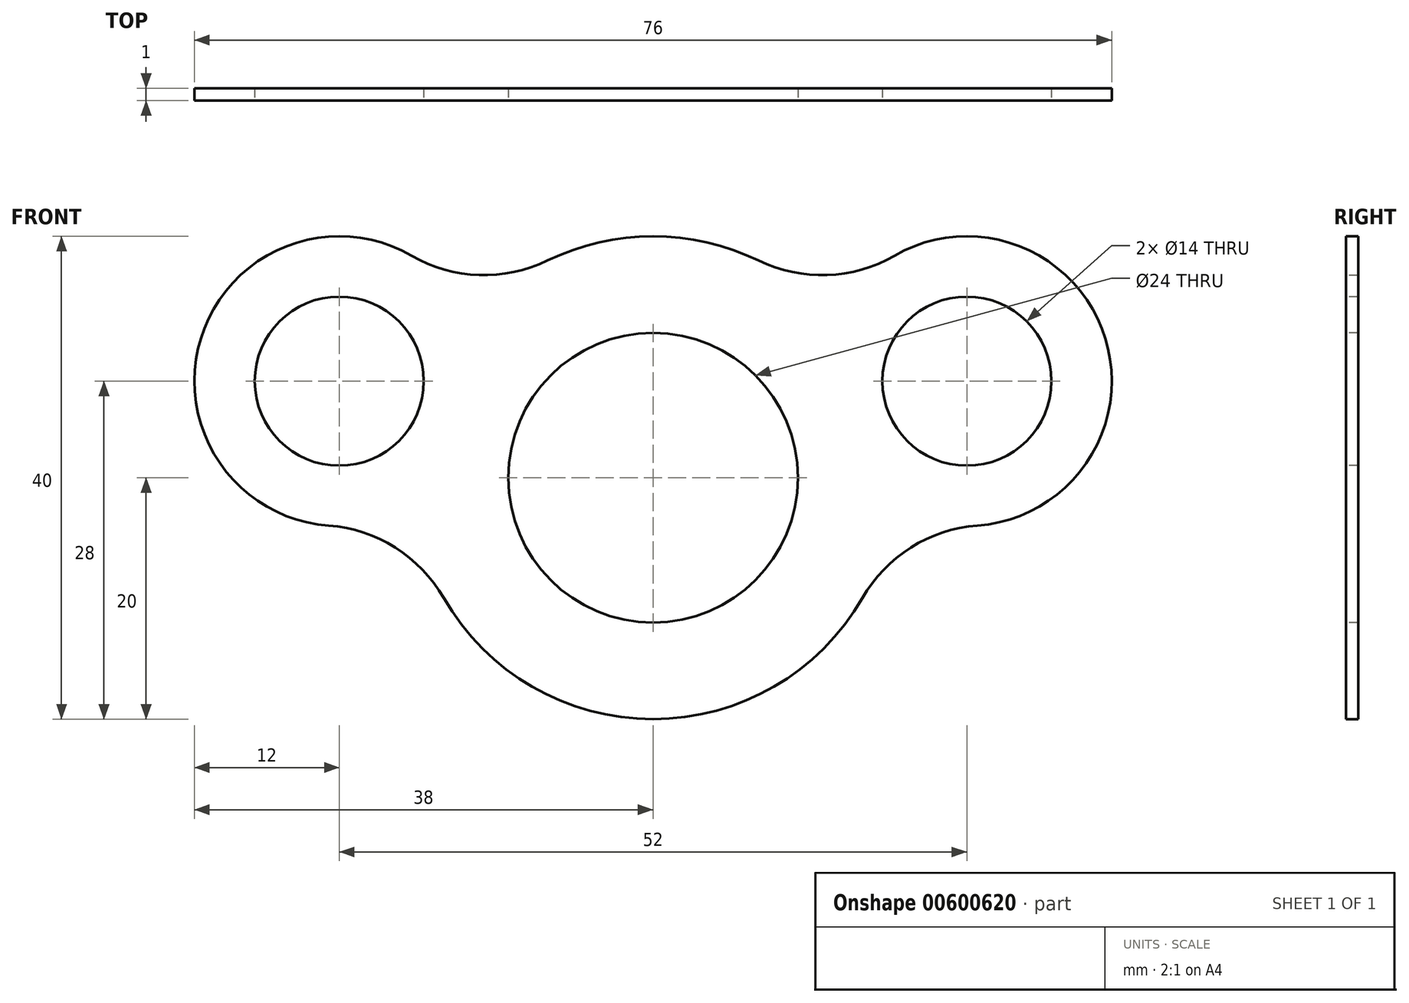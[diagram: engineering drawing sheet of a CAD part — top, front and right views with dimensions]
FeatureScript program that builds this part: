
annotation { "Feature Type Name" : "Feature", "Feature Type Description" : "" }
export const myFeature = defineFeature(function(context is Context, id is Id, definition is map)
    precondition{}
    {
        {
            var Q0;
            Q0=qCreatedBy(makeId("Front.planeOp"),FACE);
            var sketch = newSketch(context, id + "F0", { "sketchPlane" : qUnion([Q0])});
            skCircle(sketch, "E0", {"center": v(0, 0) * mm, "radius": 12 * mm});
            skArc(sketch, "E1", {"start": v(-17.34, -9.96) * mm, "mid": v(0, -20) * mm, "end": v(17.34, -9.96) * mm});
            skCircle(sketch, "E2", {"center": v(-26, 8) * mm, "radius": 7 * mm});
            skCircle(sketch, "E3", {"center": v(26, 8) * mm, "radius": 7 * mm});
            skArc(sketch, "E4", {"start": v(-20, 18.39) * mm, "mid": v(-14.42, 16.79) * mm, "end": v(-8.74, 17.99) * mm});
            skArc(sketch, "E5", {"start": v(-17.34, -9.96) * mm, "mid": v(-21.36, -5.78) * mm, "end": v(-26.87, -3.97) * mm});
            skArc(sketch, "E6", {"start": v(26.87, -3.97) * mm, "mid": v(21.36, -5.78) * mm, "end": v(17.34, -9.96) * mm});
            skArc(sketch, "E7", {"start": v(8.74, 17.99) * mm, "mid": v(14.42, 16.79) * mm, "end": v(20, 18.39) * mm});
            skArc(sketch, "E8", {"start": v(-20, 18.39) * mm, "mid": v(-37.47, 11.53) * mm, "end": v(-26.87, -3.97) * mm});
            skArc(sketch, "E9", {"start": v(26.87, -3.97) * mm, "mid": v(37.47, 11.53) * mm, "end": v(20, 18.39) * mm});
            skArc(sketch, "E10.trimOffspring", {"start": v(8.74, 17.99) * mm, "mid": v(0, 20) * mm, "end": v(-8.74, 17.99) * mm});
            skSolve(sketch);
        }
        {
            var Q0;
            Q0=makeQuery(id+"F0.imprint","IMPRINT",FACE,{"disambiguationData":[TD([[makeQuery(id+"F0.imprint","IMPRINT",EDGE,{"derivedFrom":sQuery(id+"F0.wireOp",EDGE,"E0")}),-1.0]])]});
            extrude(context, id + "F1", {"entities" : qUnion([Q0]), "oppositeDirection" : true, "depth" : 1 * mm, "offsetDistance" : 25 * mm});
        }
    });
